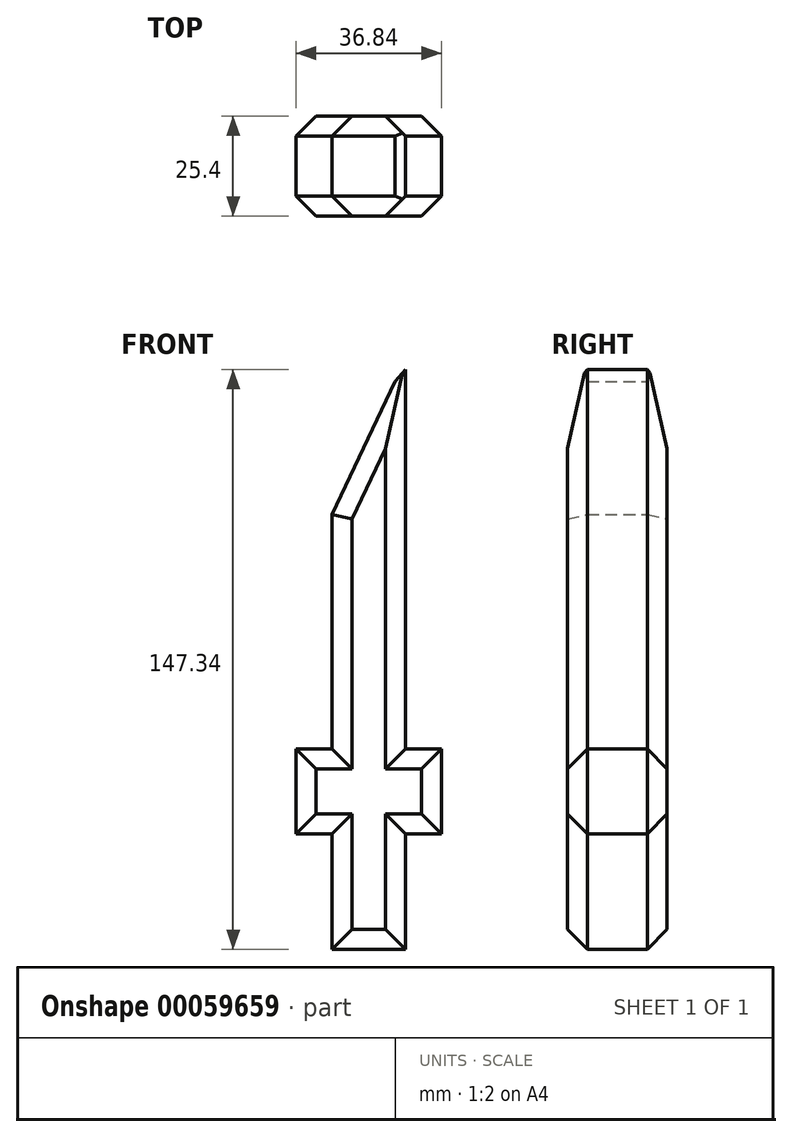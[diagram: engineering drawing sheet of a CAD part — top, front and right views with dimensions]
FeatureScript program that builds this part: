
annotation { "Feature Type Name" : "Feature", "Feature Type Description" : "" }
export const myFeature = defineFeature(function(context is Context, id is Id, definition is map)
    precondition{}
    {
        {
            var Q0;
            Q0=qCreatedBy(makeId("Front.planeOp"),FACE);
            var sketch = newSketch(context, id + "F0", { "sketchPlane" : qUnion([Q0])});
            skLineSegment(sketch, "E0.bottom", {"start": v(-9.33, -75.94) * mm, "end": v(0, -75.94) * mm});
            skLineSegment(sketch, "E0.top", {"start": v(-9.33, -46.52) * mm, "end": v(0, -46.52) * mm});
            skLineSegment(sketch, "E0.left", {"start": v(-9.33, -75.94) * mm, "end": v(-9.33, -46.52) * mm});
            skLineSegment(sketch, "E0.right", {"start": v(0, -75.94) * mm, "end": v(0, -46.52) * mm});
            skLineSegment(sketch, "E1.MirrorCS", {"start": v(9.33, -75.94) * mm, "end": v(9.33, -46.52) * mm});
            skLineSegment(sketch, "E2.MirrorCS", {"start": v(9.33, -46.52) * mm, "end": v(0, -46.52) * mm});
            skLineSegment(sketch, "E3.MirrorCS", {"start": v(9.33, -75.94) * mm, "end": v(0, -75.94) * mm});
            skLineSegment(sketch, "E4.bottom", {"start": v(-9.33, -46.52) * mm, "end": v(-18.42, -46.52) * mm});
            skLineSegment(sketch, "E4.top", {"start": v(-9.33, -25) * mm, "end": v(-18.42, -25) * mm});
            skLineSegment(sketch, "E4.left", {"start": v(-9.33, -46.52) * mm, "end": v(-9.33, -25) * mm});
            skLineSegment(sketch, "E4.right", {"start": v(-18.42, -46.52) * mm, "end": v(-18.42, -25) * mm});
            skLineSegment(sketch, "E5.MirrorCS", {"start": v(9.33, -46.52) * mm, "end": v(9.33, -25) * mm});
            skLineSegment(sketch, "E6.MirrorCS", {"start": v(9.33, -25) * mm, "end": v(18.42, -25) * mm});
            skLineSegment(sketch, "E7.MirrorCS", {"start": v(9.33, -46.52) * mm, "end": v(18.42, -46.52) * mm});
            skLineSegment(sketch, "E8.MirrorCS", {"start": v(18.42, -46.52) * mm, "end": v(18.42, -25) * mm});
            skLineSegment(sketch, "E9", {"start": v(-9.33, -25) * mm, "end": v(-9.33, 34.56) * mm});
            skLineSegment(sketch, "E10.MirrorCS", {"start": v(9.33, -25) * mm, "end": v(9.33, 34.56) * mm});
            skLineSegment(sketch, "E11", {"start": v(-9.33, 34.56) * mm, "end": v(6.7, 68.29) * mm});
            skLineSegment(sketch, "E12", {"start": v(9.33, 34.56) * mm, "end": v(9.33, 71.4) * mm});
            skLineSegment(sketch, "E13", {"start": v(6.7, 68.29) * mm, "end": v(9.33, 71.4) * mm});
            skSolve(sketch);
        }
        {
            var Q0;
            Q0=makeQuery(id+"F0.imprint","IMPRINT",FACE,{"disambiguationData":[TD([[makeQuery(id+"F0.imprint","IMPRINT",EDGE,{"derivedFrom":sQuery(id+"F0.wireOp",EDGE,"E4.bottom")}),-1.0]])]});
            var Q1;
            Q1=makeQuery(id+"F0.imprint","IMPRINT",FACE,{"disambiguationData":[TD([[makeQuery(id+"F0.imprint","IMPRINT",EDGE,{"derivedFrom":sQuery(id+"F0.wireOp",EDGE,"E0.top")}),1.0]])]});
            var Q2;
            Q2=makeQuery(id+"F0.imprint","IMPRINT",FACE,{"disambiguationData":[TD([[makeQuery(id+"F0.imprint","IMPRINT",EDGE,{"derivedFrom":sQuery(id+"F0.wireOp",EDGE,"E5.MirrorCS")}),-1.0]])]});
            var Q3;
            Q3=makeQuery(id+"F0.imprint","IMPRINT",FACE,{"disambiguationData":[TD([[makeQuery(id+"F0.imprint","IMPRINT",EDGE,{"derivedFrom":sQuery(id+"F0.wireOp",EDGE,"E0.bottom")}),1.0]])]});
            var Q4;
            Q4=makeQuery(id+"F0.imprint","IMPRINT",FACE,{"disambiguationData":[TD([[makeQuery(id+"F0.imprint","IMPRINT",EDGE,{"derivedFrom":sQuery(id+"F0.wireOp",EDGE,"E0.right")}),-1.0]])]});
            extrude(context, id + "F1", {"entities" : qUnion([Q0, Q1, Q2, Q3, Q4]), "depth" : 25.4 * mm});
        }
        {
            var Q0;
            Q0=qCreatedBy(makeId("Front.planeOp"),FACE);
            var sketch = newSketch(context, id + "F2", { "sketchPlane" : qUnion([Q0])});
            skCircle(sketch, "E14", {"center": v(0, -37.2) * mm, "radius": 9.56 * mm});
            skSolve(sketch);
        }
        {
            var Q0;
            Q0=makeQuery(id+"F2.imprint","IMPRINT",FACE,{"disambiguationData":[TD([[makeQuery(id+"F2.imprint","IMPRINT",EDGE,{"derivedFrom":sQuery(id+"F2.wireOp",EDGE,"E14")}),1.0]])]});
            extrude(context, id + "F3", {"entities" : qUnion([Q0]), "operationType" : NewBodyOperationType.ADD, "depth" : 25.4 * mm});
        }
        {
            var Q0;
            Q0=makeQuery(id+"F1.opExtrude","CAP_FACE",FACE,{"disambiguationData":[OSD([sQuery(id+"F0.wireOp",EDGE,"E0.bottom"),sQuery(id+"F0.wireOp",EDGE,"E0.left"),sQuery(id+"F0.wireOp",EDGE,"E1.MirrorCS"),sQuery(id+"F0.wireOp",EDGE,"E3.MirrorCS"),sQuery(id+"F0.wireOp",EDGE,"E4.bottom"),sQuery(id+"F0.wireOp",EDGE,"E4.top"),sQuery(id+"F0.wireOp",EDGE,"E4.right"),sQuery(id+"F0.wireOp",EDGE,"E6.MirrorCS"),sQuery(id+"F0.wireOp",EDGE,"E7.MirrorCS"),sQuery(id+"F0.wireOp",EDGE,"E8.MirrorCS"),sQuery(id+"F0.wireOp",EDGE,"E9"),sQuery(id+"F0.wireOp",EDGE,"E10.MirrorCS"),sQuery(id+"F0.wireOp",EDGE,"E11"),sQuery(id+"F0.wireOp",EDGE,"E12"),sQuery(id+"F0.wireOp",EDGE,"E13")])],"isStart":true});
            chamfer(context, id + "F4", {"entities" : qUnion([Q0]), "width" : 5.08 * mm, "tangentPropagation" : true});
        }
        {
            var Q0;
            Q0=makeQuery(id+"F1.opExtrude","CAP_FACE",FACE,{"disambiguationData":[OSD([sQuery(id+"F0.wireOp",EDGE,"E0.bottom"),sQuery(id+"F0.wireOp",EDGE,"E0.left"),sQuery(id+"F0.wireOp",EDGE,"E1.MirrorCS"),sQuery(id+"F0.wireOp",EDGE,"E3.MirrorCS"),sQuery(id+"F0.wireOp",EDGE,"E4.bottom"),sQuery(id+"F0.wireOp",EDGE,"E4.top"),sQuery(id+"F0.wireOp",EDGE,"E4.right"),sQuery(id+"F0.wireOp",EDGE,"E6.MirrorCS"),sQuery(id+"F0.wireOp",EDGE,"E7.MirrorCS"),sQuery(id+"F0.wireOp",EDGE,"E8.MirrorCS"),sQuery(id+"F0.wireOp",EDGE,"E9"),sQuery(id+"F0.wireOp",EDGE,"E10.MirrorCS"),sQuery(id+"F0.wireOp",EDGE,"E11"),sQuery(id+"F0.wireOp",EDGE,"E12"),sQuery(id+"F0.wireOp",EDGE,"E13")])],"isStart":false});
            chamfer(context, id + "F5", {"entities" : qUnion([Q0]), "width" : 5.08 * mm, "tangentPropagation" : true});
        }
    });
